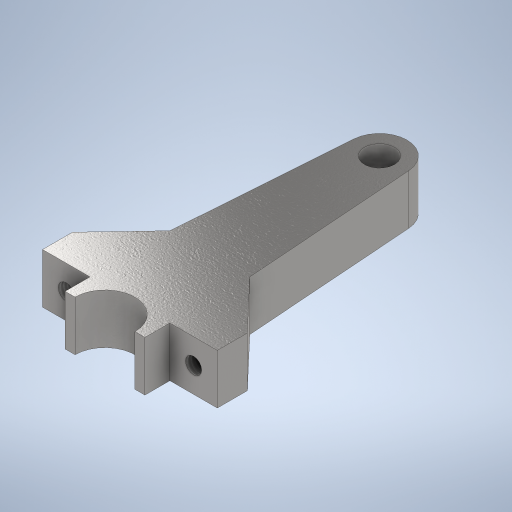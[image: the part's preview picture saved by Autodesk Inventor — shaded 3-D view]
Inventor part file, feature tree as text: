
AUTODESK INVENTOR PART (.ipt)
format: ipt  version: 2024 (Build 280153000, 153)  size: 317,952 bytes
history: native  units: mm
features: sketch x4, extrude x2, hole x2
ambient origin geometry x8: Origin, YZ Plane, XZ Plane, XY Plane, X Axis, Y Axis, Z Axis, Center Point
bodies: Volumenkörper1 (feature_tree)
feature tree (8):
  extrude  "Extrusion1"  Depth=16.0mm
  extrude  "Extrusion2"  Depth=5.0mm
  hole  "Bohrung1"  [1 undecoded]
  hole  "Bohrung2"  [1 undecoded]
  sketch  "Skizze1"  dims[d6=60.5mm d7=16.0mm]
  sketch  "Skizze2"  dims[d8=5.0mm d9=11.0mm]
  sketch  "Skizze3"  dims[d10=35.0mm d11=11.0mm]
  sketch  "Skizze4"  dims[d12=21.0mm d13=10.0mm d14=0.0mm d15=12.0mm d16=10.0mm d17=0.0mm d18=25.5mm d19=3.242mm d20=5.0mm d21=4.0mm d22=2.0mm d23=90.0deg d24=9.0mm d25=20.594885mm d26=6.02mm d27=5.0mm d28=4.0mm d29=2.0mm d30=90.0deg d31=9.0mm d32=0.0mm]
note: 2 required parameter values undecoded (feature->parameter linkage not recoverable at this tier; creation-order binding heuristic only, values carry confidence <= 0.55)
